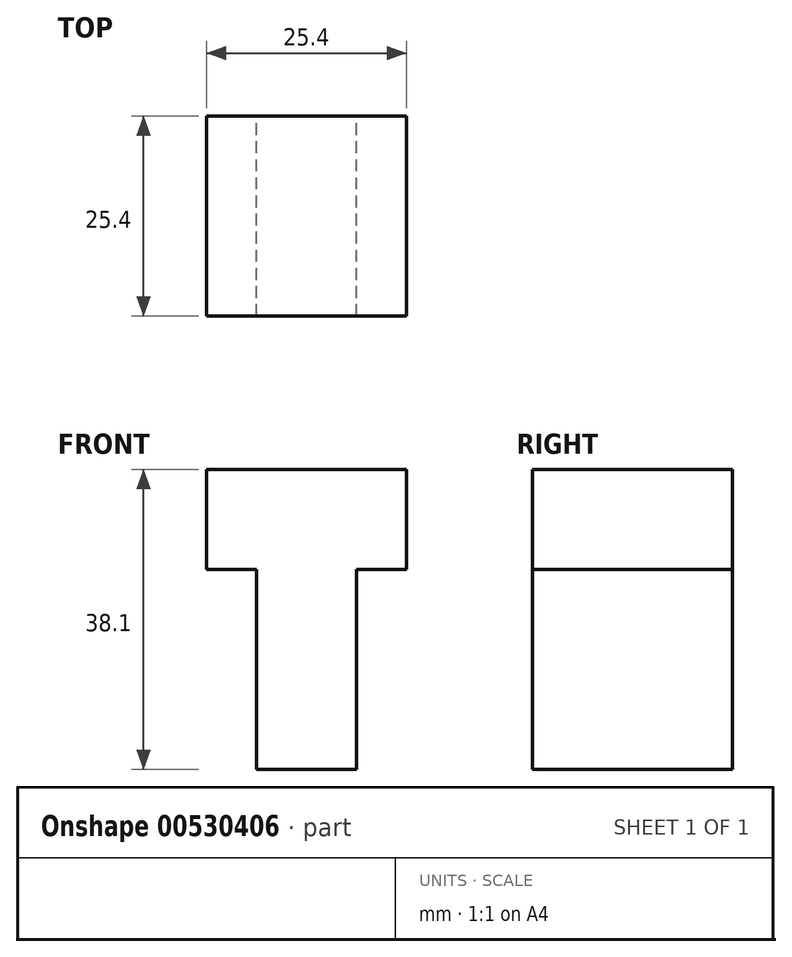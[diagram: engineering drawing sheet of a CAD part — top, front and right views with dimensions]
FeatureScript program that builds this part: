
annotation { "Feature Type Name" : "Feature", "Feature Type Description" : "" }
export const myFeature = defineFeature(function(context is Context, id is Id, definition is map)
    precondition{}
    {
        {
            var Q0;
            Q0=qCreatedBy(makeId("Front.planeOp"),FACE);
            var sketch = newSketch(context, id + "F0", { "sketchPlane" : qUnion([Q0])});
            skLineSegment(sketch, "E0", {"start": v(-16.72, 28.74) * mm, "end": v(8.68, 28.74) * mm});
            skLineSegment(sketch, "E1", {"start": v(-16.72, 28.74) * mm, "end": v(-16.72, 16.04) * mm});
            skLineSegment(sketch, "E2", {"start": v(-16.72, 16.04) * mm, "end": v(-10.37, 16.04) * mm});
            skLineSegment(sketch, "E3", {"start": v(2.33, 16.04) * mm, "end": v(8.68, 16.04) * mm});
            skLineSegment(sketch, "E4", {"start": v(2.33, 16.04) * mm, "end": v(2.33, -9.36) * mm});
            skLineSegment(sketch, "E5", {"start": v(-10.37, 16.04) * mm, "end": v(-10.37, -9.36) * mm});
            skLineSegment(sketch, "E6", {"start": v(-10.37, -9.36) * mm, "end": v(2.33, -9.36) * mm});
            skLineSegment(sketch, "E7", {"start": v(8.68, 28.74) * mm, "end": v(8.68, 16.04) * mm});
            skSolve(sketch);
        }
        {
            var Q0;
            Q0=makeQuery(id+"F0.imprint","IMPRINT",FACE,{"disambiguationData":[TD([[makeQuery(id+"F0.imprint","IMPRINT",EDGE,{"derivedFrom":sQuery(id+"F0.wireOp",EDGE,"E0")}),-1.0]])]});
            extrude(context, id + "F1", {"entities" : qUnion([Q0]), "depth" : 25.4 * mm, "offsetDistance" : 25.4 * mm});
        }
    });
